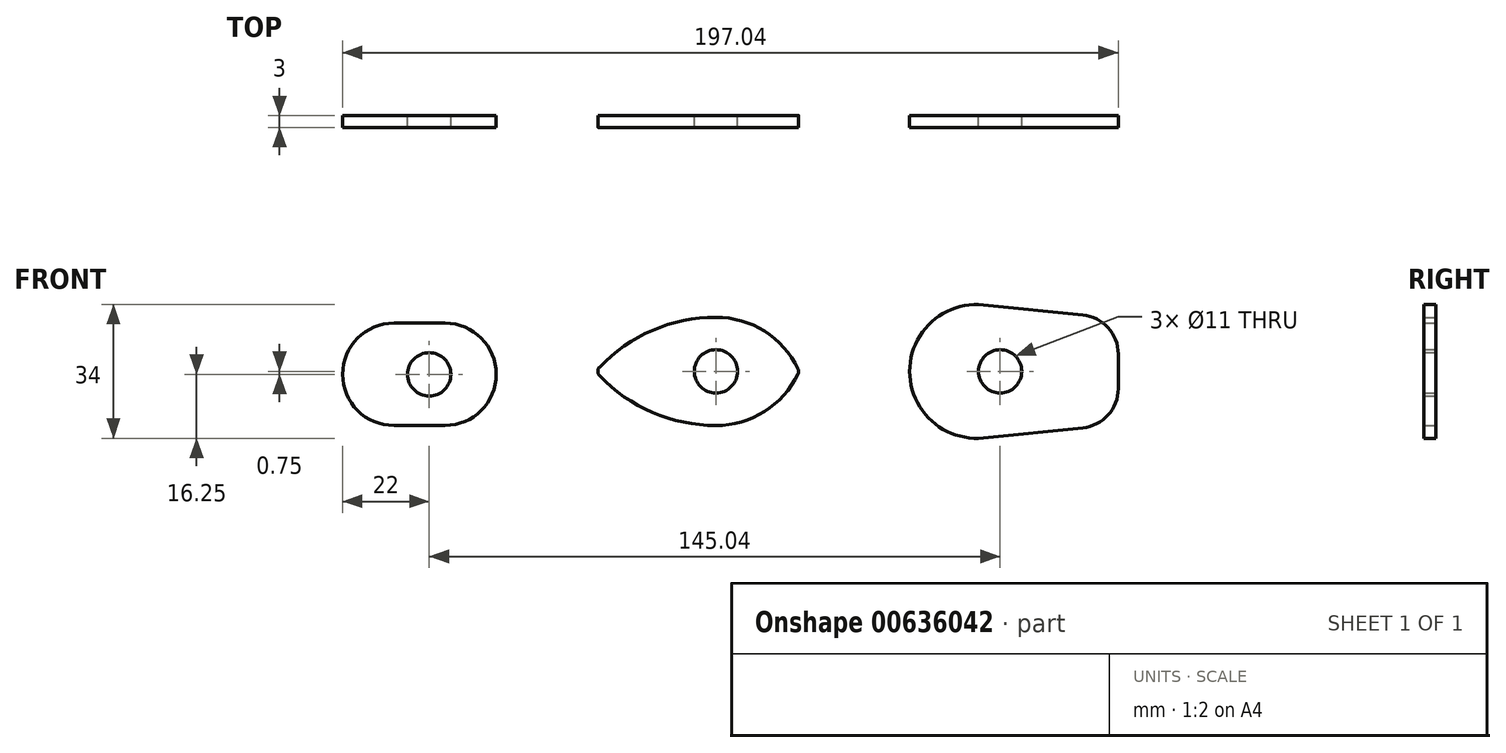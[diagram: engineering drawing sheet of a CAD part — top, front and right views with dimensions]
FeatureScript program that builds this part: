
annotation { "Feature Type Name" : "Feature", "Feature Type Description" : "" }
export const myFeature = defineFeature(function(context is Context, id is Id, definition is map)
    precondition{}
    {
        {
            var Q0;
            Q0=qCreatedBy(makeId("Front.planeOp"),FACE);
            var sketch = newSketch(context, id + "F0", { "sketchPlane" : qUnion([Q0])});
            skLineSegment(sketch, "E0.bottom", {"start": v(13, 0) * mm, "end": v(26, 0) * mm});
            skLineSegment(sketch, "E0.top", {"start": v(13, 26) * mm, "end": v(26, 26) * mm});
            skLineSegment(sketch, "E1", {"start": v(0, 13) * mm, "end": v(39, 13) * mm, "construction": true});
            skLineSegment(sketch, "E2", {"start": v(22, 26) * mm, "end": v(22, 0) * mm, "construction": true});
            skCircle(sketch, "E3", {"center": v(22, 13) * mm, "radius": 5.5 * mm});
            skArc(sketch, "E4", {"start": v(13, 26) * mm, "mid": v(0, 13) * mm, "end": v(13, 0) * mm});
            skArc(sketch, "E5", {"start": v(26, 0) * mm, "mid": v(39, 13) * mm, "end": v(26, 26) * mm});
            skPoint(sketch, "E6.orphan", {"position": v(0, 26) * mm});
            skPoint(sketch, "E7.orphan", {"position": v(39, 0) * mm});
            skPoint(sketch, "E0.right.end.orphan", {"position": v(39, 26) * mm});
            skCircle(sketch, "E8", {"center": v(94.84, 13.75) * mm, "radius": 5.5 * mm});
            skLineSegment(sketch, "E9", {"start": v(64.84, 13.75) * mm, "end": v(115.84, 13.75) * mm, "construction": true});
            skArc(sketch, "E10", {"start": v(94.84, 27.5) * mm, "mid": v(78.73, 24.19) * mm, "end": v(65.25, 14.78) * mm});
            skArc(sketch, "E11", {"start": v(115.69, 14.4) * mm, "mid": v(107.15, 23.95) * mm, "end": v(94.84, 27.5) * mm});
            skArc(sketch, "E12", {"start": v(65.25, 14.78) * mm, "mid": v(64.94, 14.3) * mm, "end": v(64.84, 13.75) * mm});
            skArc(sketch, "E13", {"start": v(115.84, 13.75) * mm, "mid": v(115.8, 14.08) * mm, "end": v(115.69, 14.4) * mm});
            skPoint(sketch, "E14.orphan", {"position": v(64.84, 27.5) * mm});
            skPoint(sketch, "E15.bottom.start.orphan", {"position": v(64.84, 0) * mm});
            skPoint(sketch, "E16.orphan", {"position": v(94.84, 0) * mm});
            skArc(sketch, "E17.MirrorCS", {"start": v(65.25, 12.72) * mm, "mid": v(64.94, 13.2) * mm, "end": v(64.84, 13.75) * mm});
            skArc(sketch, "E18.MirrorCS", {"start": v(94.84, 0) * mm, "mid": v(78.73, 3.31) * mm, "end": v(65.25, 12.72) * mm});
            skArc(sketch, "E19.MirrorCS", {"start": v(115.69, 13.1) * mm, "mid": v(107.15, 3.55) * mm, "end": v(94.84, 0) * mm});
            skArc(sketch, "E20.MirrorCS", {"start": v(115.84, 13.75) * mm, "mid": v(115.8, 13.42) * mm, "end": v(115.69, 13.1) * mm});
            skLineSegment(sketch, "E21", {"start": v(144.04, 13.75) * mm, "end": v(197.04, 13.75) * mm, "construction": true});
            skLineSegment(sketch, "E22", {"start": v(139.8, 30.75) * mm, "end": v(202.46, 30.75) * mm, "construction": true});
            skArc(sketch, "E23", {"start": v(162.75, 30.66) * mm, "mid": v(149.64, 26.36) * mm, "end": v(144.04, 13.75) * mm});
            skLineSegment(sketch, "E24", {"start": v(197.04, 13.75) * mm, "end": v(197.04, 18.15) * mm});
            skArc(sketch, "E25", {"start": v(197.04, 18.15) * mm, "mid": v(194.46, 24.85) * mm, "end": v(188.05, 28.1) * mm});
            skLineSegment(sketch, "E26", {"start": v(162.75, 30.66) * mm, "end": v(188.05, 28.1) * mm});
            skArc(sketch, "E27.trimOffspring", {"start": v(178.04, 13.8) * mm, "mid": v(178.05, 13.77) * mm, "end": v(178.06, 13.75) * mm});
            skArc(sketch, "E28.trimOffspring", {"start": v(178.04, 13.75) * mm, "mid": v(178.04, 13.77) * mm, "end": v(178.04, 13.8) * mm});
            skCircle(sketch, "E29", {"center": v(167.04, 13.75) * mm, "radius": 5.5 * mm});
            skLineSegment(sketch, "E30.MirrorCS", {"start": v(197.04, 13.75) * mm, "end": v(197.04, 9.35) * mm});
            skLineSegment(sketch, "E31.MirrorCS", {"start": v(162.75, -3.16) * mm, "end": v(188.05, -0.6) * mm});
            skArc(sketch, "E32.MirrorCS", {"start": v(162.75, -3.16) * mm, "mid": v(149.64, 1.14) * mm, "end": v(144.04, 13.75) * mm});
            skArc(sketch, "E33.MirrorCS", {"start": v(197.04, 9.35) * mm, "mid": v(194.46, 2.65) * mm, "end": v(188.05, -0.6) * mm});
            skSolve(sketch);
        }
        {
            var Q0;
            Q0 = qSketchRegion(id + "F0", true);
            extrude(context, id + "F1", {"entities" : qUnion([Q0]), "depth" : 3 * mm, "offsetDistance" : 25 * mm});
        }
    });
